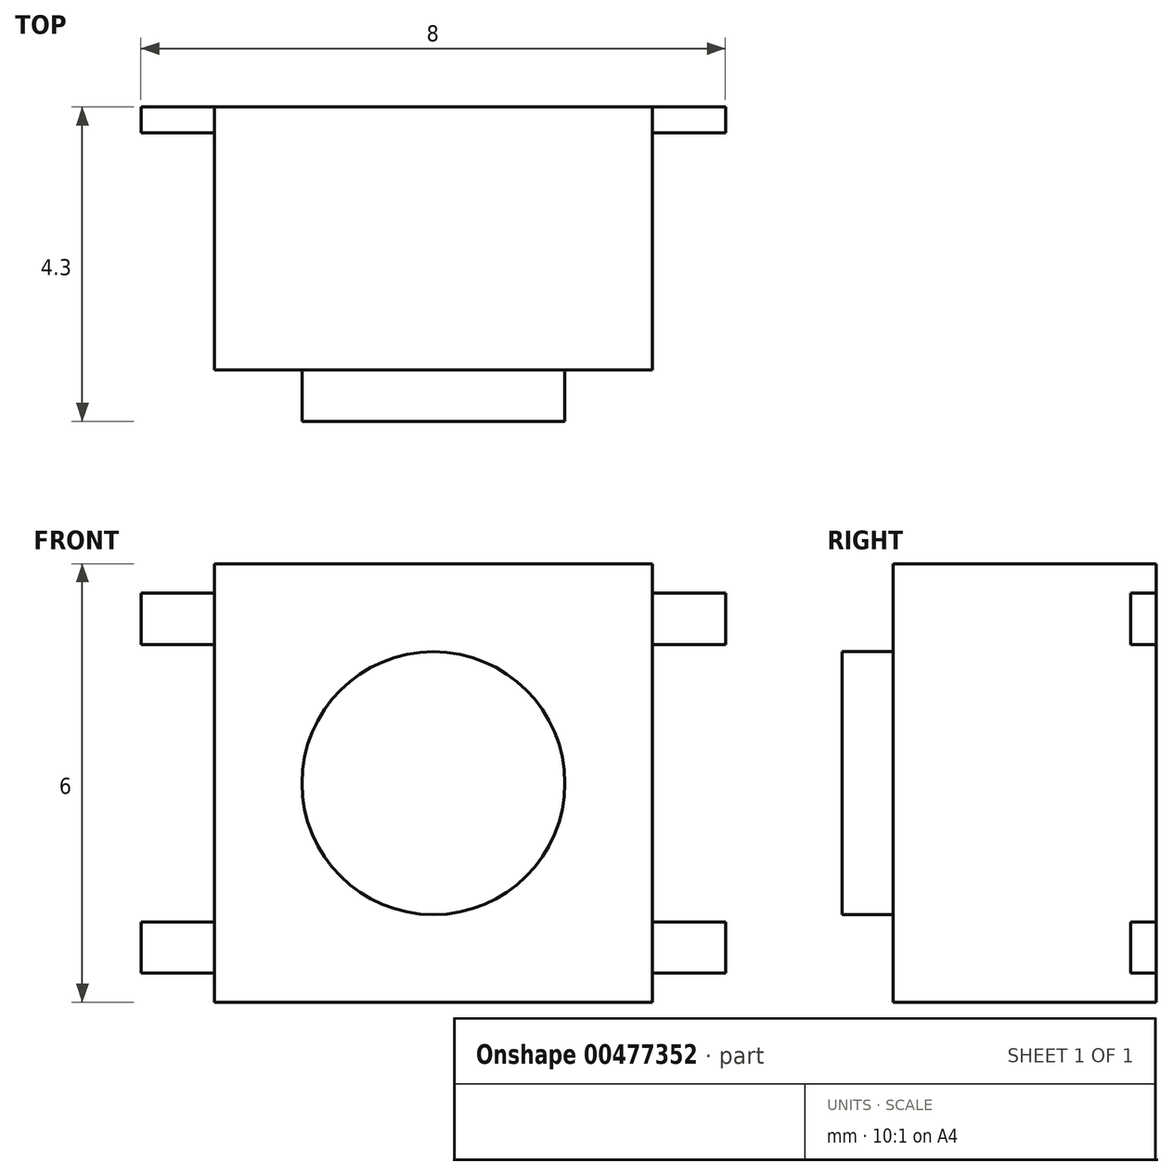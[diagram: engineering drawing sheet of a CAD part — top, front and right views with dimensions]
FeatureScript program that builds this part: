
annotation { "Feature Type Name" : "Feature", "Feature Type Description" : "" }
export const myFeature = defineFeature(function(context is Context, id is Id, definition is map)
    precondition{}
    {
        {
            var Q0;
            Q0=qCreatedBy(makeId("Front.planeOp"),FACE);
            var sketch = newSketch(context, id + "F0", { "sketchPlane" : qUnion([Q0])});
            skLineSegment(sketch, "E0.bottom", {"start": v(-57.38, 38.62) * mm, "end": v(-51.38, 38.62) * mm});
            skLineSegment(sketch, "E0.top", {"start": v(-57.38, 32.62) * mm, "end": v(-51.38, 32.62) * mm});
            skLineSegment(sketch, "E0.left", {"start": v(-57.38, 38.62) * mm, "end": v(-57.38, 32.62) * mm});
            skLineSegment(sketch, "E0.right", {"start": v(-51.38, 38.62) * mm, "end": v(-51.38, 32.62) * mm});
            skSolve(sketch);
        }
        {
            var Q0;
            Q0 = qSketchRegion(id + "F0", true);
            extrude(context, id + "F1", {"entities" : qUnion([Q0]), "depth" : 3.6 * mm});
        }
        {
            var Q0;
            Q0=makeQuery(id+"F1.opExtrude","CAP_FACE",FACE,{"disambiguationData":[OSD([sQuery(id+"F0.wireOp",EDGE,"E0.bottom"),sQuery(id+"F0.wireOp",EDGE,"E0.top"),sQuery(id+"F0.wireOp",EDGE,"E0.left"),sQuery(id+"F0.wireOp",EDGE,"E0.right")])],"isStart":false});
            var sketch = newSketch(context, id + "F2", { "sketchPlane" : qUnion([Q0])});
            skCircle(sketch, "E1", {"center": v(-54.38, 35.62) * mm, "radius": 1.8 * mm});
            skPoint(sketch, "E1.centerSnap0", {"position": v(-57.38, 35.62) * mm});
            skPoint(sketch, "E1.centerSnap1", {"position": v(-54.38, 38.62) * mm});
            skSolve(sketch);
        }
        {
            var Q0;
            Q0 = qSketchRegion(id + "F2", true);
            extrude(context, id + "F3", {"entities" : qUnion([Q0]), "operationType" : NewBodyOperationType.ADD, "depth" : 0.7 * mm});
        }
        {
            var Q0;
            Q0=makeQuery(id+"F1.opExtrude","SWEPT_FACE",FACE,{"disambiguationData":[OSD([sQuery(id+"F0.wireOp",EDGE,"E0.left")])]});
            var sketch = newSketch(context, id + "F4", { "sketchPlane" : qUnion([Q0])});
            skLineSegment(sketch, "E2.bottom", {"start": v(0, 38.22) * mm, "end": v(0.35, 38.22) * mm});
            skLineSegment(sketch, "E2.top", {"start": v(0, 37.52) * mm, "end": v(0.35, 37.52) * mm});
            skLineSegment(sketch, "E2.left", {"start": v(0, 38.22) * mm, "end": v(0, 37.52) * mm});
            skLineSegment(sketch, "E2.right", {"start": v(0.35, 38.22) * mm, "end": v(0.35, 37.52) * mm});
            skLineSegment(sketch, "E3.bottom", {"start": v(0, 33.72) * mm, "end": v(0.35, 33.72) * mm});
            skLineSegment(sketch, "E3.top", {"start": v(0, 33.02) * mm, "end": v(0.35, 33.02) * mm});
            skLineSegment(sketch, "E3.left", {"start": v(0, 33.72) * mm, "end": v(0, 33.02) * mm});
            skLineSegment(sketch, "E3.right", {"start": v(0.35, 33.72) * mm, "end": v(0.35, 33.02) * mm});
            skSolve(sketch);
        }
        {
            var Q0;
            Q0 = qSketchRegion(id + "F4", true);
            extrude(context, id + "F5", {"entities" : qUnion([Q0]), "operationType" : NewBodyOperationType.ADD, "depth" : 1 * mm, "hasSecondDirection" : true, "secondDirectionOppositeDirection" : true, "secondDirectionDepth" : 7 * mm});
        }
    });
